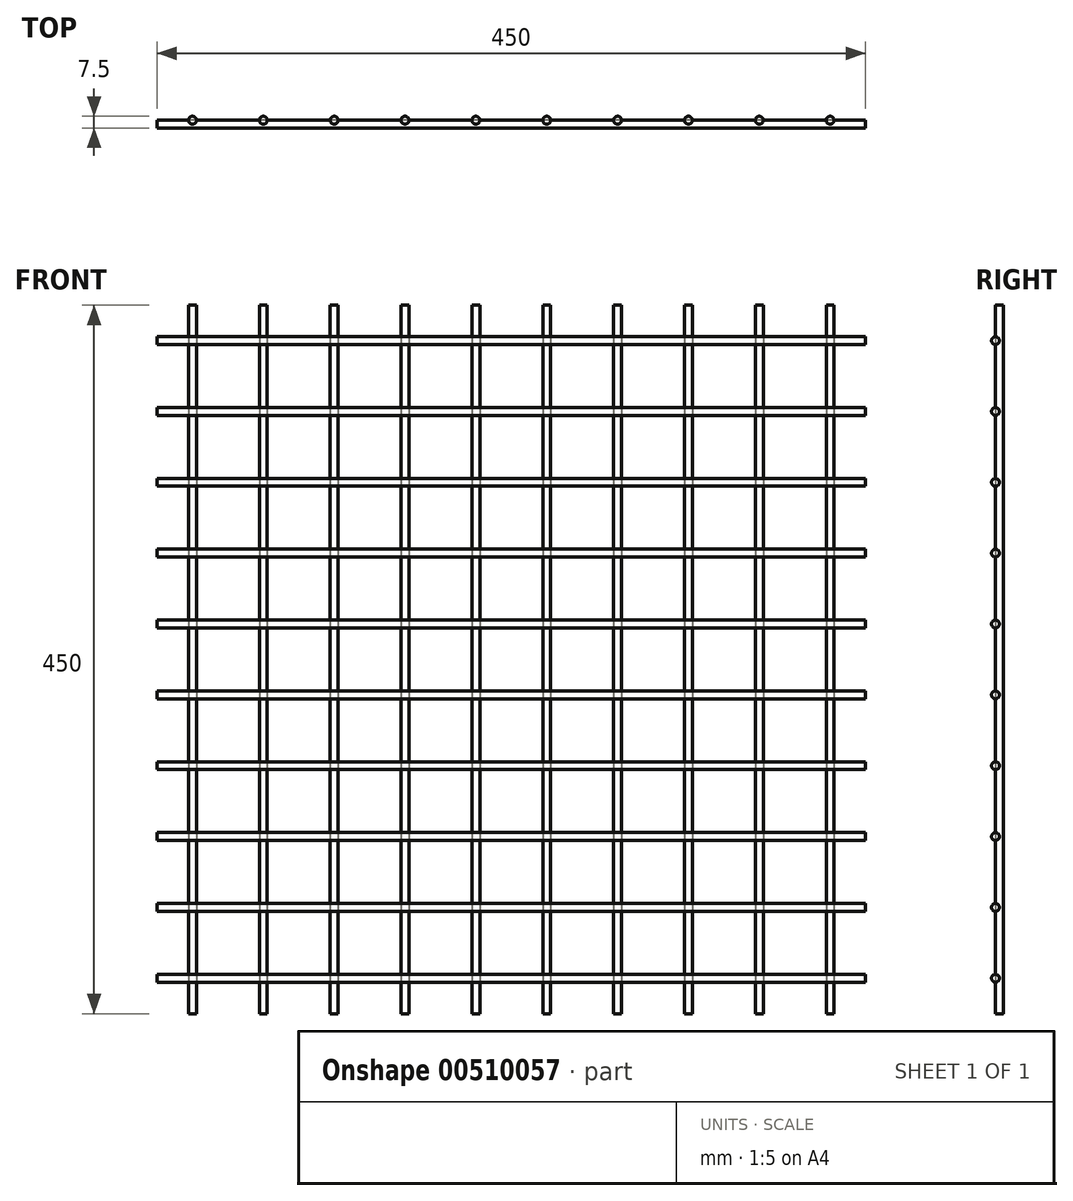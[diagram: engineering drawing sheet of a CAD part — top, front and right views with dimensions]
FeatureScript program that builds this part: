
annotation { "Feature Type Name" : "Feature", "Feature Type Description" : "" }
export const myFeature = defineFeature(function(context is Context, id is Id, definition is map)
    precondition{}
    {
        {
            var Q0;
            Q0=qCreatedBy(makeId("Right.planeOp"),FACE);
            var sketch = newSketch(context, id + "F0", { "sketchPlane" : qUnion([Q0])});
            skCircle(sketch, "E0", {"center": v(0, 22.5) * mm, "radius": 2.5 * mm});
            skCircle(sketch, "E1.0.1.0", {"center": v(0, 67.5) * mm, "radius": 2.5 * mm});
            skCircle(sketch, "E1.0.2.0", {"center": v(0, 112.5) * mm, "radius": 2.5 * mm});
            skCircle(sketch, "E1.0.3.0", {"center": v(0, 157.5) * mm, "radius": 2.5 * mm});
            skCircle(sketch, "E1.0.4.0", {"center": v(0, 202.5) * mm, "radius": 2.5 * mm});
            skCircle(sketch, "E1.0.5.0", {"center": v(0, 247.5) * mm, "radius": 2.5 * mm});
            skCircle(sketch, "E1.0.6.0", {"center": v(0, 292.5) * mm, "radius": 2.5 * mm});
            skCircle(sketch, "E1.0.7.0", {"center": v(0, 337.5) * mm, "radius": 2.5 * mm});
            skCircle(sketch, "E1.0.8.0", {"center": v(0, 382.5) * mm, "radius": 2.5 * mm});
            skLineSegment(sketch, "E1.direction1", {"start": v(0, 22.5) * mm, "end": v(25, 22.5) * mm, "construction": true});
            skLineSegment(sketch, "E1.direction2", {"start": v(0, 22.5) * mm, "end": v(0, 67.5) * mm, "construction": true});
            skCircle(sketch, "E2.0.0.9", {"center": v(0, 427.5) * mm, "radius": 2.5 * mm});
            skSolve(sketch);
        }
        {
            var Q0;
            Q0 = qSketchRegion(id + "F0", true);
            extrude(context, id + "F1", {"entities" : qUnion([Q0]), "endBound" : BoundingType.SYMMETRIC, "depth" : 450 * mm});
        }
        {
            var Q0;
            Q0=qCreatedBy(makeId("Top.planeOp"),FACE);
            var sketch = newSketch(context, id + "F2", { "sketchPlane" : qUnion([Q0])});
            skCircle(sketch, "E3", {"center": v(-202.5, 2.5) * mm, "radius": 2.5 * mm});
            skCircle(sketch, "E4.1.0.0", {"center": v(-157.5, 2.5) * mm, "radius": 2.5 * mm});
            skCircle(sketch, "E4.2.0.0", {"center": v(-112.5, 2.5) * mm, "radius": 2.5 * mm});
            skCircle(sketch, "E4.3.0.0", {"center": v(-67.5, 2.5) * mm, "radius": 2.5 * mm});
            skCircle(sketch, "E4.4.0.0", {"center": v(-22.5, 2.5) * mm, "radius": 2.5 * mm});
            skCircle(sketch, "E4.5.0.0", {"center": v(22.5, 2.5) * mm, "radius": 2.5 * mm});
            skLineSegment(sketch, "E4.direction1", {"start": v(-202.5, 2.5) * mm, "end": v(-157.5, 2.5) * mm, "construction": true});
            skCircle(sketch, "E5.0.6.0", {"center": v(67.5, 2.5) * mm, "radius": 2.5 * mm});
            skCircle(sketch, "E5.0.7.0", {"center": v(112.5, 2.5) * mm, "radius": 2.5 * mm});
            skCircle(sketch, "E5.0.8.0", {"center": v(157.5, 2.5) * mm, "radius": 2.5 * mm});
            skCircle(sketch, "E6.0.9.0", {"center": v(202.5, 2.5) * mm, "radius": 2.5 * mm});
            skSolve(sketch);
        }
        {
            var Q0;
            Q0 = qSketchRegion(id + "F2", true);
            extrude(context, id + "F3", {"entities" : qUnion([Q0]), "depth" : 450 * mm});
        }
    });
